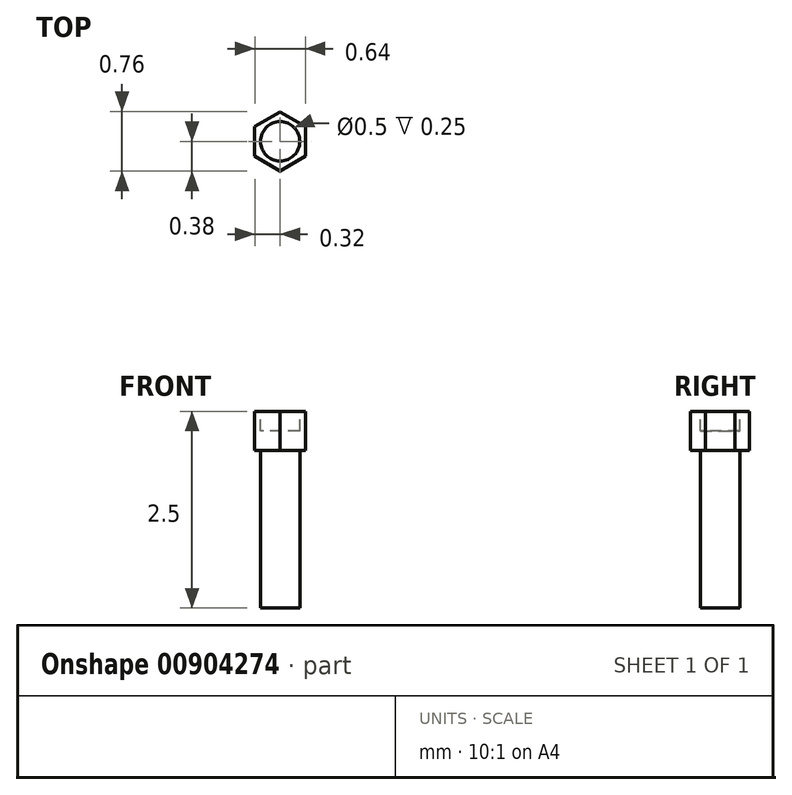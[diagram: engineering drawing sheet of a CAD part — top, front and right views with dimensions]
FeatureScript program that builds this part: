
annotation { "Feature Type Name" : "Feature", "Feature Type Description" : "" }
export const myFeature = defineFeature(function(context is Context, id is Id, definition is map)
    precondition{}
    {
        {
            var Q0;
            Q0=qCreatedBy(makeId("Front.planeOp"),FACE);
            var sketch = newSketch(context, id + "F0", { "sketchPlane" : qUnion([Q0])});
            skLineSegment(sketch, "E0.bottom", {"start": v(0, 0) * mm, "end": v(-0.25, 0) * mm});
            skLineSegment(sketch, "E0.top", {"start": v(0, 2) * mm, "end": v(-0.25, 2) * mm});
            skLineSegment(sketch, "E0.left", {"start": v(0, 0) * mm, "end": v(0, 2) * mm});
            skLineSegment(sketch, "E0.right", {"start": v(-0.25, 0) * mm, "end": v(-0.25, 2) * mm});
            skSolve(sketch);
        }
        {
            var Q0;
            Q0=makeQuery(id+"F0.imprint","IMPRINT",FACE,{"disambiguationData":[TD([[makeQuery(id+"F0.imprint","IMPRINT",EDGE,{"derivedFrom":sQuery(id+"F0.wireOp",EDGE,"E0.bottom")}),-1.0]])]});
            var Q1;
            Q1=sQuery(id+"F0.wireOp",EDGE,"E0.left");
            revolve(context, id + "F1", {"surfaceOperationType" : NewSurfaceOperationType.NEW, "entities" : qUnion([Q0]), "axis" : qUnion([Q1]), "revolveType" : RevolveType.FULL});
        }
        {
            var Q0;
            Q0=makeQuery(id+"F1.opRevolve","SWEPT_FACE",FACE,{"disambiguationData":[OSD([sQuery(id+"F0.wireOp",EDGE,"E0.top")])]});
            var sketch = newSketch(context, id + "F2", { "sketchPlane" : qUnion([Q0])});
            skCircle(sketch, "E1.cCircle", {"center": v(0, 0) * mm, "radius": 0.38 * mm, "construction": true});
            skLineSegment(sketch, "E1.0", {"start": v(0, 0.38) * mm, "end": v(0.32, 0.19) * mm});
            skLineSegment(sketch, "E1.1", {"start": v(0.32, 0.19) * mm, "end": v(0.32, -0.19) * mm});
            skLineSegment(sketch, "E1.2", {"start": v(0.32, -0.19) * mm, "end": v(0, -0.37) * mm});
            skLineSegment(sketch, "E1.3", {"start": v(0, -0.38) * mm, "end": v(-0.32, -0.19) * mm});
            skLineSegment(sketch, "E1.4", {"start": v(-0.32, -0.19) * mm, "end": v(-0.32, 0.19) * mm});
            skLineSegment(sketch, "E1.5", {"start": v(-0.32, 0.19) * mm, "end": v(0, 0.38) * mm});
            skSolve(sketch);
        }
        {
            var Q0;
            Q0=makeQuery(id+"F2.imprint","IMPRINT",FACE,{"disambiguationData":[TD([[makeQuery(id+"F2.imprint","IMPRINT",EDGE,{"derivedFrom":sQuery(id+"F2.wireOp",EDGE,"E1.0")}),-1.0]])]});
            var Q1;
            Q1=makeQuery(id+"F2.imprint","IMPRINT",FACE,{"disambiguationData":[TD([[makeQuery(id+"F2.imprint","IMPRINT",EDGE,{"derivedFrom":makeQuery(id+"F1.opRevolve","SWEPT_EDGE",EDGE,{"disambiguationData":[OSD([sQuery(id+"F0.wireOp",EDGE,"E0.top"),sQuery(id+"F0.wireOp",EDGE,"E0.right")])]})}),-1.0]])]});
            extrude(context, id + "F3", {"entities" : qUnion([Q0, Q1]), "operationType" : NewBodyOperationType.ADD, "depth" : 0.5 * mm, "offsetDistance" : 25 * mm});
        }
        {
            var Q0;
            Q0=makeQuery(id+"F3.opExtrude","CAP_FACE",FACE,{"disambiguationData":[OSD([sQuery(id+"F2.wireOp",EDGE,"E1.0"),sQuery(id+"F2.wireOp",EDGE,"E1.1"),sQuery(id+"F2.wireOp",EDGE,"E1.2"),sQuery(id+"F2.wireOp",EDGE,"E1.3"),sQuery(id+"F2.wireOp",EDGE,"E1.4"),sQuery(id+"F2.wireOp",EDGE,"E1.5")])],"isStart":false});
            var sketch = newSketch(context, id + "F4", { "sketchPlane" : qUnion([Q0])});
            skCircle(sketch, "E2", {"center": v(0, 0) * mm, "radius": 0.25 * mm});
            skSolve(sketch);
        }
        {
            var Q0;
            Q0=makeQuery(id+"F4.imprint","IMPRINT",FACE,{"disambiguationData":[TD([[makeQuery(id+"F4.imprint","IMPRINT",EDGE,{"derivedFrom":sQuery(id+"F4.wireOp",EDGE,"E2")}),1.0]])]});
            extrude(context, id + "F5", {"entities" : qUnion([Q0]), "operationType" : NewBodyOperationType.REMOVE, "oppositeDirection" : true, "depth" : 0.25 * mm, "offsetDistance" : 25 * mm});
        }
    });
